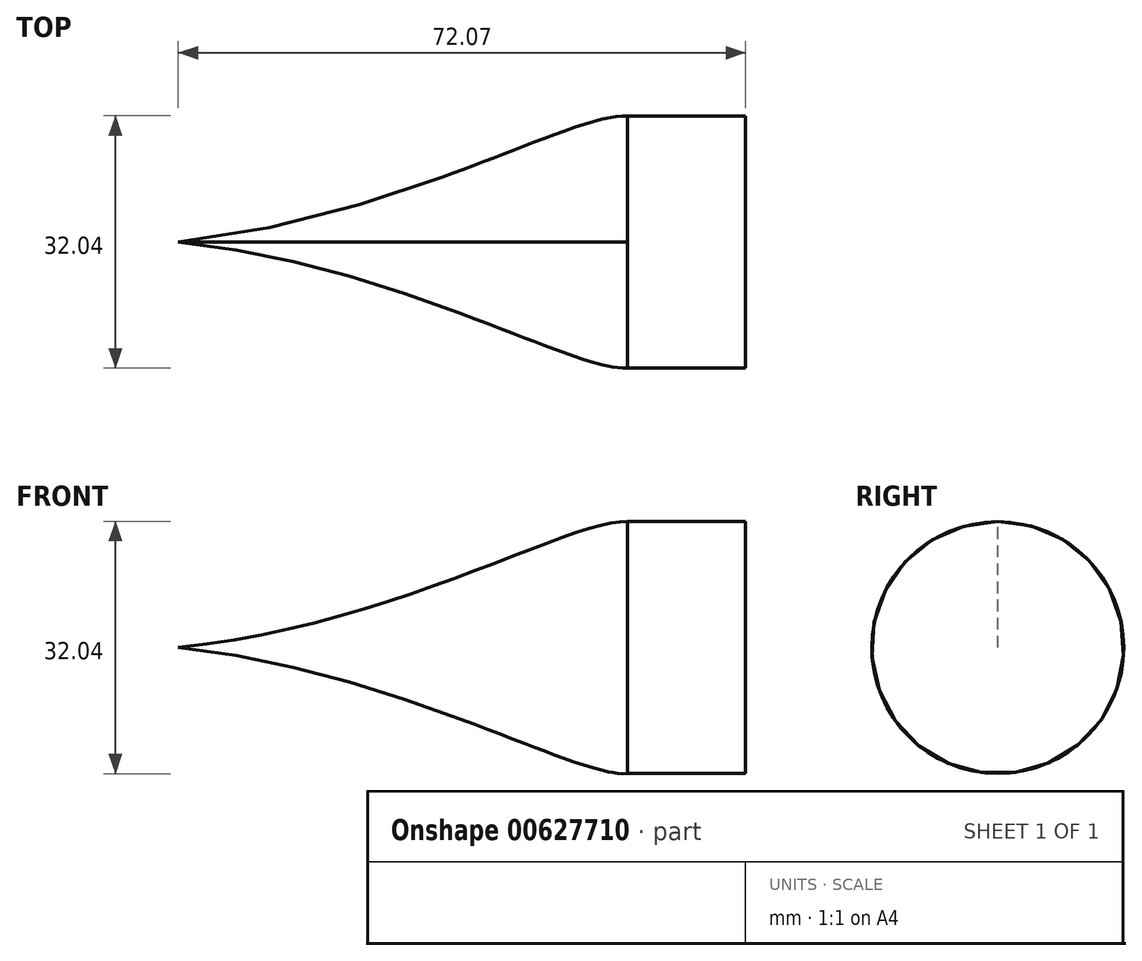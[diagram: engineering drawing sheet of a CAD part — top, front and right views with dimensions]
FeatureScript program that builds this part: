
annotation { "Feature Type Name" : "Feature", "Feature Type Description" : "" }
export const myFeature = defineFeature(function(context is Context, id is Id, definition is map)
    precondition{}
    {
        {
            var Q0;
            Q0=qCreatedBy(makeId("Front.planeOp"),FACE);
            var sketch = newSketch(context, id + "F0", { "sketchPlane" : qUnion([Q0])});
            skLineSegment(sketch, "E0", {"start": v(0, 0) * mm, "end": v(-57.07, 0) * mm});
            skLineSegment(sketch, "E1", {"start": v(0, 0) * mm, "end": v(0, 16) * mm});
            skFitSpline(sketch, "E2", {"points": [v(-57.07, 0) * mm, v(0, 16) * mm], "startDerivative": vector(83.51, 8.7) * mm, "endDerivative": vector(20.57, -1.64) * mm});
            skSolve(sketch);
        }
        {
            var Q0;
            Q0 = qSketchRegion(id + "F0", true);
            var Q1;
            Q1=sQuery(id+"F0.wireOp",EDGE,"E0");
            revolve(context, id + "F1", {"entities" : qUnion([Q0]), "axis" : qUnion([Q1]), "revolveType" : RevolveType.FULL});
        }
        {
            var Q0;
            Q0=qCreatedBy(makeId("Right.planeOp"),FACE);
            var sketch = newSketch(context, id + "F2", { "sketchPlane" : qUnion([Q0])});
            skCircle(sketch, "E3", {"center": v(0, 0) * mm, "radius": 16 * mm});
            skSolve(sketch);
        }
        {
            var Q0;
            Q0=makeQuery(id+"F2.imprint","IMPRINT",FACE,{"disambiguationData":[TD([[makeQuery(id+"F2.imprint","IMPRINT",EDGE,{"derivedFrom":sQuery(id+"F2.wireOp",EDGE,"E3")}),1.0]])]});
            extrude(context, id + "F3", {"entities" : qUnion([Q0]), "operationType" : NewBodyOperationType.ADD, "depth" : 15 * mm, "offsetDistance" : 25 * mm});
        }
    });
